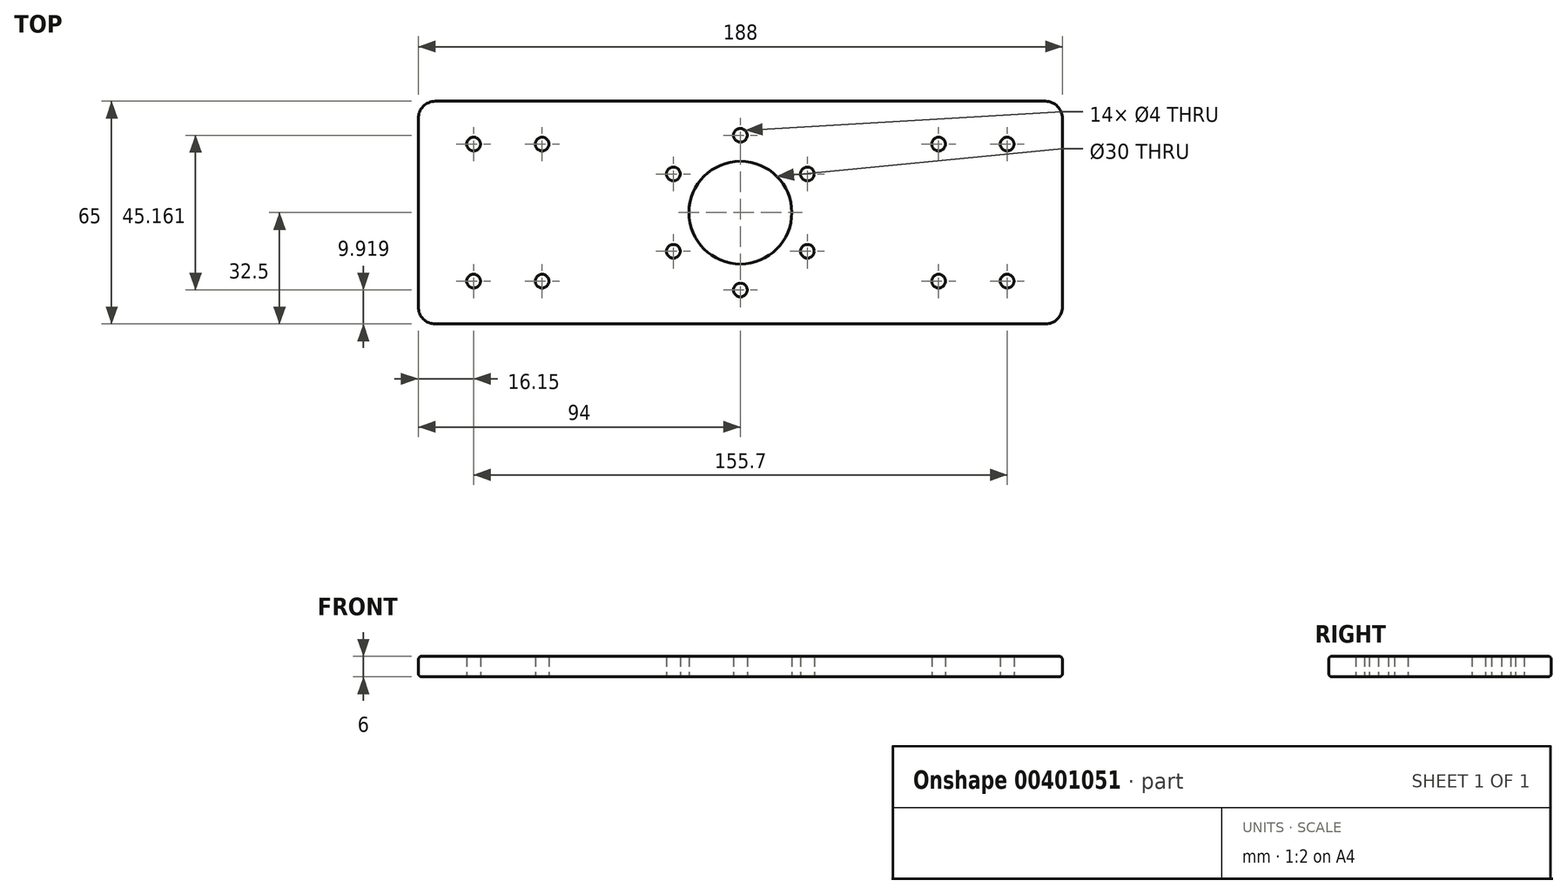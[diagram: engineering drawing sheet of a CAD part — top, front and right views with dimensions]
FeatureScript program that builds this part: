
annotation { "Feature Type Name" : "Feature", "Feature Type Description" : "" }
export const myFeature = defineFeature(function(context is Context, id is Id, definition is map)
    precondition{}
    {
        {
            var Q0;
            Q0=qCreatedBy(makeId("Top.planeOp"),FACE);
            var sketch = newSketch(context, id + "F0", { "sketchPlane" : qUnion([Q0])});
            skLineSegment(sketch, "E0.bottom", {"start": v(-89, 32.5) * mm, "end": v(89, 32.5) * mm});
            skLineSegment(sketch, "E0.top", {"start": v(-89, -32.5) * mm, "end": v(89, -32.5) * mm});
            skLineSegment(sketch, "E0.left", {"start": v(-94, 27.5) * mm, "end": v(-94, -27.5) * mm});
            skLineSegment(sketch, "E0.right", {"start": v(94, 27.5) * mm, "end": v(94, -27.5) * mm});
            skCircle(sketch, "E1", {"center": v(-77.85, 20) * mm, "radius": 2 * mm});
            skCircle(sketch, "E2", {"center": v(-77.85, -20) * mm, "radius": 2 * mm});
            skCircle(sketch, "E3", {"center": v(77.85, -20) * mm, "radius": 2 * mm});
            skCircle(sketch, "E4", {"center": v(77.85, 20) * mm, "radius": 2 * mm});
            skPoint(sketch, "E5.visualSharp", {"position": v(-94, 32.5) * mm});
            skArc(sketch, "E5.filletArc", {"start": v(-89, 32.5) * mm, "mid": v(-92.54, 31.04) * mm, "end": v(-94, 27.5) * mm});
            skPoint(sketch, "E6.visualSharp", {"position": v(-94, -32.5) * mm});
            skArc(sketch, "E6.filletArc", {"start": v(-94, -27.5) * mm, "mid": v(-92.54, -31.04) * mm, "end": v(-89, -32.5) * mm});
            skPoint(sketch, "E7.visualSharp", {"position": v(94, -32.5) * mm});
            skArc(sketch, "E7.filletArc", {"start": v(89, -32.5) * mm, "mid": v(92.54, -31.04) * mm, "end": v(94, -27.5) * mm});
            skPoint(sketch, "E8.visualSharp", {"position": v(94, 32.5) * mm});
            skArc(sketch, "E8.filletArc", {"start": v(94, 27.5) * mm, "mid": v(92.54, 31.04) * mm, "end": v(89, 32.5) * mm});
            skCircle(sketch, "E9", {"center": v(-57.85, 20) * mm, "radius": 2 * mm});
            skCircle(sketch, "E10", {"center": v(-57.85, -20) * mm, "radius": 2 * mm});
            skCircle(sketch, "E11", {"center": v(57.85, 20) * mm, "radius": 2 * mm});
            skCircle(sketch, "E12", {"center": v(57.85, -20) * mm, "radius": 2 * mm});
            skCircle(sketch, "E13", {"center": v(0, 22.58) * mm, "radius": 2 * mm});
            skCircle(sketch, "E14.1.0", {"center": v(-19.56, 11.3) * mm, "radius": 2 * mm});
            skCircle(sketch, "E14.2.0", {"center": v(-19.56, -11.3) * mm, "radius": 2 * mm});
            skPoint(sketch, "E14.center", {"position": v(0, 0) * mm});
            skCircle(sketch, "E15.1.3.0", {"center": v(0, -22.58) * mm, "radius": 2 * mm});
            skCircle(sketch, "E15.1.4.0", {"center": v(19.56, -11.3) * mm, "radius": 2 * mm});
            skCircle(sketch, "E15.1.5.0", {"center": v(19.56, 11.3) * mm, "radius": 2 * mm});
            skCircle(sketch, "E16", {"center": v(0, 0) * mm, "radius": 15 * mm});
            skSolve(sketch);
        }
        {
            var Q0;
            Q0=makeQuery(id+"F0.imprint","IMPRINT",FACE,{"disambiguationData":[TD([[makeQuery(id+"F0.imprint","IMPRINT",EDGE,{"derivedFrom":sQuery(id+"F0.wireOp",EDGE,"E0.bottom")}),-1.0]])]});
            extrude(context, id + "F1", {"entities" : qUnion([Q0]), "depth" : 6 * mm});
        }
        {
            var Q0;
            Q0=makeQuery(id+"F1.opExtrude","CAP_EDGE",EDGE,{"disambiguationData":[OSD([sQuery(id+"F0.wireOp",EDGE,"E0.left")])],"isStart":false});
            var Q1;
            Q1=makeQuery(id+"F1.opExtrude","SWEPT_FACE",FACE,{"disambiguationData":[OSD([sQuery(id+"F0.wireOp",EDGE,"E5.filletArc")])]});
            var Q2;
            Q2=makeQuery(id+"F1.opExtrude","SWEPT_FACE",FACE,{"disambiguationData":[OSD([sQuery(id+"F0.wireOp",EDGE,"E0.left")])]});
            var Q3;
            Q3=makeQuery(id+"F1.opExtrude","SWEPT_FACE",FACE,{"disambiguationData":[OSD([sQuery(id+"F0.wireOp",EDGE,"E6.filletArc")])]});
            var Q4;
            Q4=makeQuery(id+"F1.opExtrude","CAP_EDGE",EDGE,{"disambiguationData":[OSD([sQuery(id+"F0.wireOp",EDGE,"E0.top")])],"isStart":false});
            var Q5;
            Q5=makeQuery(id+"F1.opExtrude","CAP_EDGE",EDGE,{"disambiguationData":[OSD([sQuery(id+"F0.wireOp",EDGE,"E0.top")])],"isStart":true});
            var Q6;
            Q6=makeQuery(id+"F1.opExtrude","SWEPT_FACE",FACE,{"disambiguationData":[OSD([sQuery(id+"F0.wireOp",EDGE,"E0.top")])]});
            var Q7;
            Q7=makeQuery(id+"F1.opExtrude","SWEPT_FACE",FACE,{"disambiguationData":[OSD([sQuery(id+"F0.wireOp",EDGE,"E7.filletArc")])]});
            var Q8;
            Q8=makeQuery(id+"F1.opExtrude","SWEPT_FACE",FACE,{"disambiguationData":[OSD([sQuery(id+"F0.wireOp",EDGE,"E0.right")])]});
            var Q9;
            Q9=makeQuery(id+"F1.opExtrude","SWEPT_FACE",FACE,{"disambiguationData":[OSD([sQuery(id+"F0.wireOp",EDGE,"E0.bottom")])]});
            var Q10;
            Q10=makeQuery(id+"F1.opExtrude","SWEPT_FACE",FACE,{"disambiguationData":[OSD([sQuery(id+"F0.wireOp",EDGE,"E8.filletArc")])]});
            fillet(context, id + "F2", {"entities" : qUnion([Q0, Q1, Q2, Q3, Q4, Q5, Q6, Q7, Q8, Q9, Q10]), "radius" : 1 * mm, "tangentPropagation" : true, "allowEdgeOverflow" : false});
        }
    });
